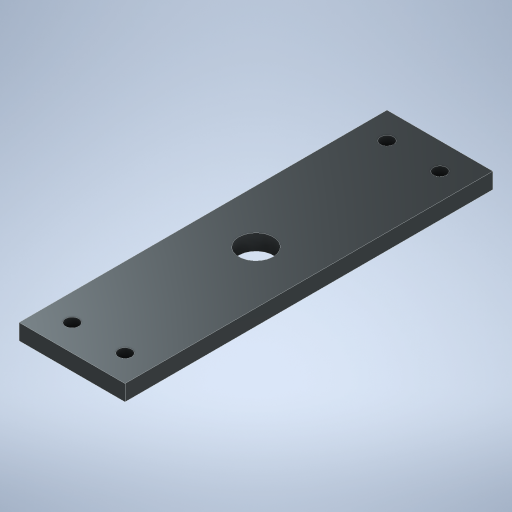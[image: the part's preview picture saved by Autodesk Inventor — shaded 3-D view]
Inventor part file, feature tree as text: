
AUTODESK INVENTOR PART (.ipt)
format: ipt  version: 2023.2 (Build 272271030, 271C)  size: 282,624 bytes
history: native  units: mm
features: hole x3, sketch x2, other x1, extrude x1
ambient origin geometry x8: Origin, YZ Plane, XZ Plane, XY Plane, X Axis, Y Axis, Z Axis, Center Point
bodies: Body1 (feature_tree)
feature tree (7):
  other  "Sólido1"
  extrude  "Extrusão1"  Depth=139.0mm
  hole  "Furo1"  [1 undecoded]
  hole  "Furo2"  [1 undecoded]
  hole  "Furo3"  [1 undecoded]
  sketch  "Esboço1"  dims[d0=40.0mm d1=139.0mm]
  sketch  "Esboço2"  dims[d2=6.0mm d3=0.0mm d4=139.0mm d5=40.0mm d6=20.0mm d7=69.5mm d8=13.0mm d9=6.0mm d10=4.0mm d11=2.0mm d12=90.0deg d13=0.5mm d14=20.594885mm d19=40.0mm d20=10.0mm d21=10.0mm d22=4.5mm d23=4.5mm d24=5.0mm d25=12.0mm d26=8.5mm d27=3.0mm d28=90.0deg d29=0.5mm d30=20.594885mm d32=0.0mm d33=4.5mm d34=0.0mm d35=31.0mm d36=31.0mm d37=31.0mm d38=31.0mm d39=31.0mm d40=31.0mm d41=31.0mm d42=4.5mm d43=0.0mm d44=4.5mm d45=40.0mm d46=10.0mm d47=10.0mm d48=10.0mm d49=10.0mm d50=5.0mm d51=6.0mm d52=3.023mm d53=2.0mm d54=14.3117mm d55=0.5mm d56=20.594885mm d57=10.0mm d58=10.0mm d59=10.0mm]
note: 3 required parameter values undecoded (feature->parameter linkage not recoverable at this tier; creation-order binding heuristic only, values carry confidence <= 0.55)
